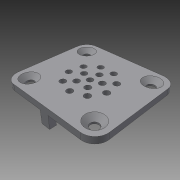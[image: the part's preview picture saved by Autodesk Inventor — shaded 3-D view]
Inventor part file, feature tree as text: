
AUTODESK INVENTOR PART (.ipt)
format: ipt  version: 2014 (Build 180170000, 170)  size: 168,448 bytes
history: native  units: mm
features: sketch x4, extrude x3, hole x1, fillet x1
ambient origin geometry x8: Origin, YZ Plane, XZ Plane, XY Plane, X Axis, Y Axis, Z Axis, Center Point
bodies: Solid1 (feature_tree)
feature tree (9):
  extrude  "Extrusion1"  Depth=47.0mm
  hole  "Hole1"  [1 undecoded]
  extrude  "Extrusion2"  Depth=4.2mm
  extrude  "Extrusion3"  Depth=3.0mm
  fillet  "Fillet1"  Radius=6.2mm
  sketch  "Sketch1"  dims[d0=43.0mm d1=47.0mm]
  sketch  "Sketch2"  dims[d2=3.0mm d3=0.0mm d4=6.5mm]
  sketch  "Sketch3"  dims[d5=6.5mm]
  sketch  "Sketch4"  dims[d6=4.0mm d7=6.0mm d8=8.5mm d9=2.0mm d10=90.0deg d11=8.0mm d12=20.594885mm d13=4.2mm d14=3.0mm d15=6.2mm d16=0.0mm d17=3.0mm d18=3.0mm d19=5.0mm d20=50.0mm d22=360.0deg d24=3.0mm d25=10.0mm d26=90.0mm d28=360.0deg d30=7.0mm d31=0.0mm d32=6.0mm]
note: 1 required parameter value undecoded (feature->parameter linkage not recoverable at this tier; creation-order binding heuristic only, values carry confidence <= 0.55)
